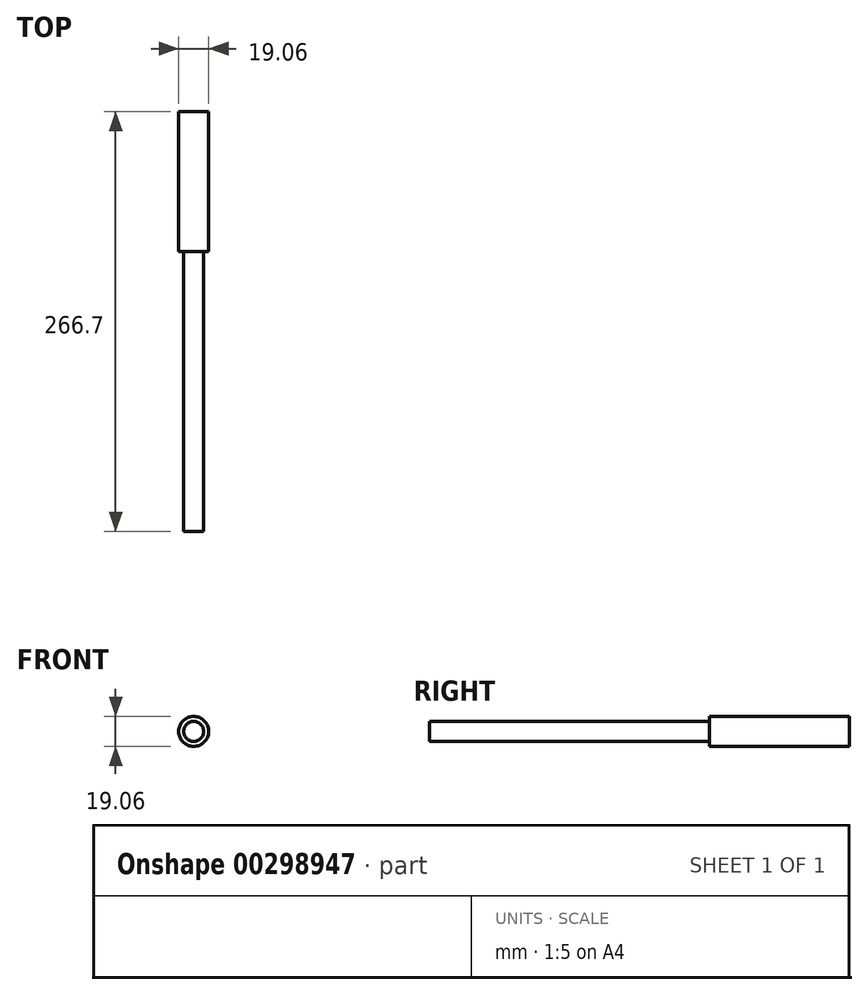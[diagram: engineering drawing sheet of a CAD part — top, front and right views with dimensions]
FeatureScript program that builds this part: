
annotation { "Feature Type Name" : "Feature", "Feature Type Description" : "" }
export const myFeature = defineFeature(function(context is Context, id is Id, definition is map)
    precondition{}
    {
        {
            var Q0;
            Q0=qCreatedBy(makeId("Front.planeOp"),FACE);
            var sketch = newSketch(context, id + "F0", { "sketchPlane" : qUnion([Q0])});
            skCircle(sketch, "E0", {"center": v(0, 0) * mm, "radius": 9.53 * mm});
            skSolve(sketch);
        }
        {
            var Q0;
            Q0 = qSketchRegion(id + "F0", true);
            extrude(context, id + "F1", {"entities" : qUnion([Q0]), "oppositeDirection" : true, "depth" : 88.9 * mm});
        }
        {
            var Q0;
            Q0=makeQuery(id+"F1.opExtrude","CAP_FACE",FACE,{"disambiguationData":[OSD([sQuery(id+"F0.wireOp",EDGE,"E0")])],"isStart":true});
            var sketch = newSketch(context, id + "F2", { "sketchPlane" : qUnion([Q0])});
            skCircle(sketch, "E1", {"center": v(0, 0) * mm, "radius": 6.35 * mm});
            skSolve(sketch);
        }
        {
            var Q0;
            Q0=makeQuery(id+"F2.imprint","IMPRINT",FACE,{"disambiguationData":[TD([[makeQuery(id+"F2.imprint","IMPRINT",EDGE,{"derivedFrom":sQuery(id+"F2.wireOp",EDGE,"E1")}),1.0]])]});
            extrude(context, id + "F3", {"entities" : qUnion([Q0]), "operationType" : NewBodyOperationType.ADD, "depth" : 177.8 * mm});
        }
    });
